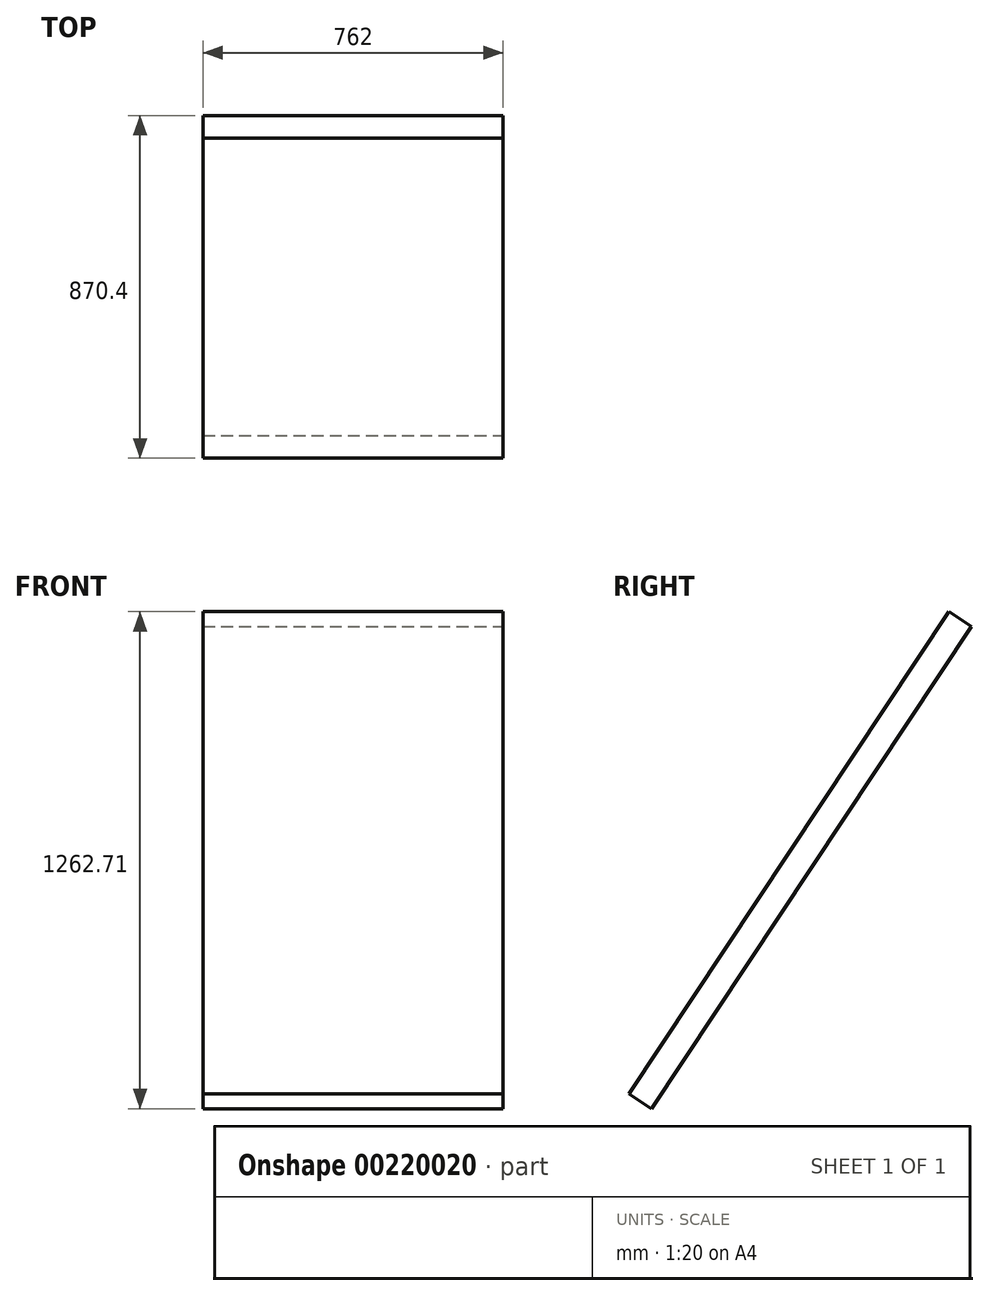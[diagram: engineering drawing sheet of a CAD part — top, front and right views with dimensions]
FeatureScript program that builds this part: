
annotation { "Feature Type Name" : "Feature", "Feature Type Description" : "" }
export const myFeature = defineFeature(function(context is Context, id is Id, definition is map)
    precondition{}
    {
        {
            var Q0;
            Q0=qCreatedBy(makeId("Right.planeOp"),FACE);
            var sketch = newSketch(context, id + "F0", { "sketchPlane" : qUnion([Q0])});
            skLineSegment(sketch, "E0", {"start": v(0, 2913.41) * mm, "end": v(-812.8, 1688.94) * mm});
            skLineSegment(sketch, "E1", {"start": v(-812.8, 1688.94) * mm, "end": v(1076.85, 1688.94) * mm, "construction": true});
            skSolve(sketch);
        }
        {
            var Q0;
            Q0=sQuery(id+"F0.wireOp",EDGE,"HXvVuCk2-IOc2-gW1W-kLZb-kXqK5PjOOn96");
            var Q1;
            Q1=sQuery(id+"F0.wireOp",EDGE,"E0");
            extrude(context, id + "F1", {"bodyType" : ToolBodyType.SURFACE, "surfaceEntities" : qUnion([Q0, Q1]), "endBound" : BoundingType.SYMMETRIC, "depth" : 762 * mm});
        }
        {
            var Q0;
            Q0=makeQuery(id+"F1.opExtrude","SWEPT_FACE",FACE,{"disambiguationData":[OSD([sQuery(id+"F0.wireOp",EDGE,"E0"),sQuery(id+"F0.wireOp",EDGE,"HXvVuCk2-IOc2-gW1W-kLZb-kXqK5PjOOn96")])]});
            extrude(context, id + "F2", {"entities" : qUnion([Q0]), "depth" : 69.14 * mm});
        }
    });
